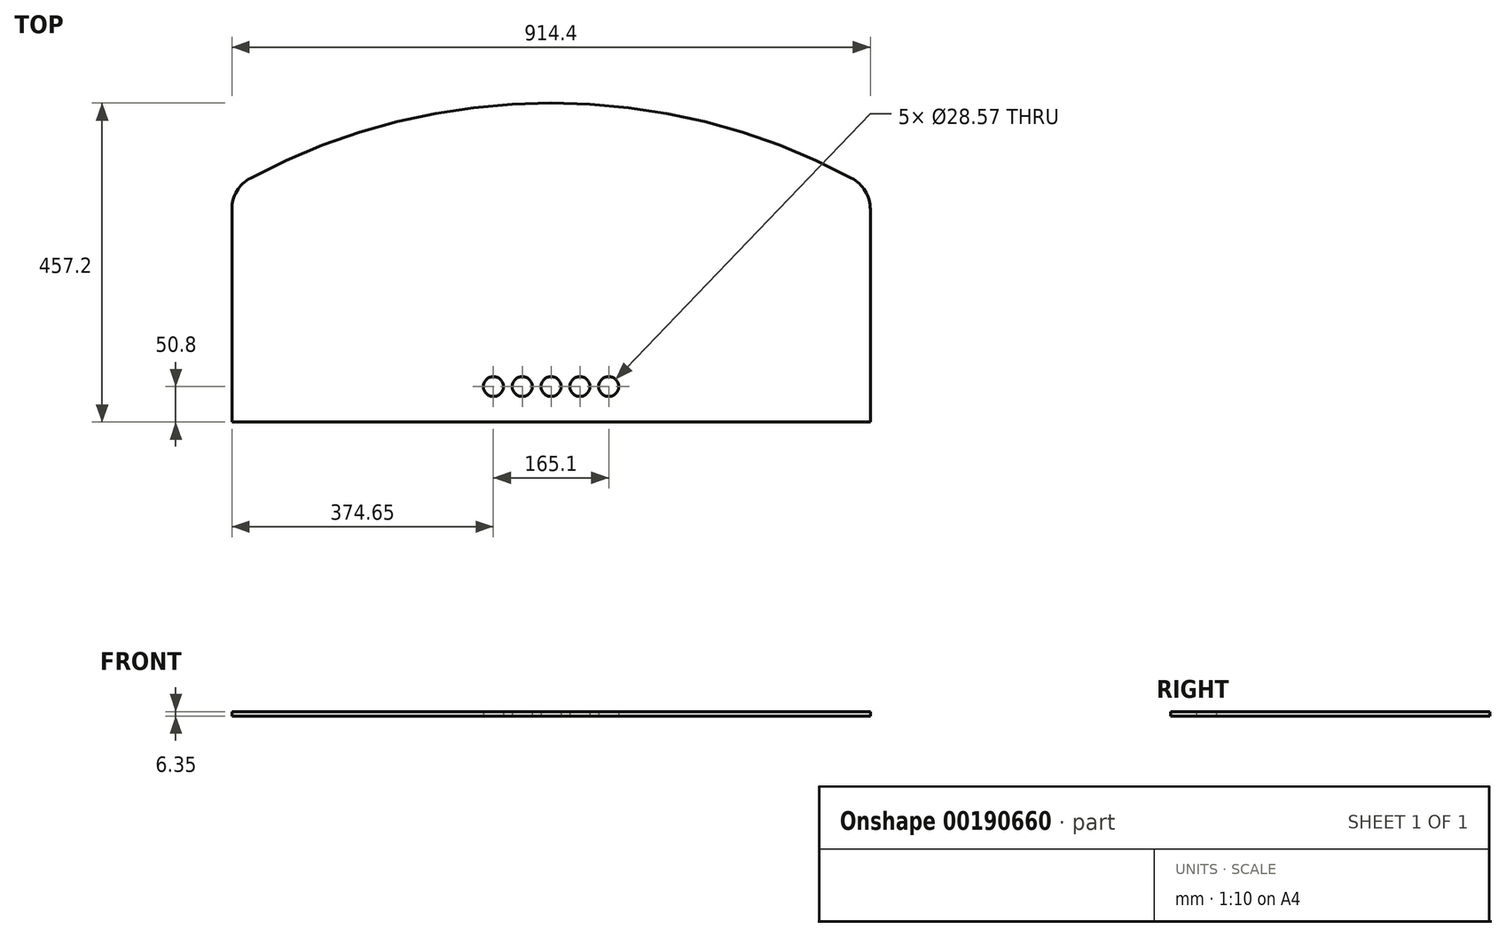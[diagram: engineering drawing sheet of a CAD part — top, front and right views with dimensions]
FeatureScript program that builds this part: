
annotation { "Feature Type Name" : "Feature", "Feature Type Description" : "" }
export const myFeature = defineFeature(function(context is Context, id is Id, definition is map)
    precondition{}
    {
        {
            var Q0;
            Q0=qCreatedBy(makeId("Top.planeOp"),FACE);
            var sketch = newSketch(context, id + "F0", { "sketchPlane" : qUnion([Q0])});
            skLineSegment(sketch, "E0.bottom", {"start": v(0, 0) * mm, "end": v(-914.4, 0) * mm});
            skLineSegment(sketch, "E0.left", {"start": v(0, 0) * mm, "end": v(0, 304.8) * mm});
            skLineSegment(sketch, "E0.right", {"start": v(-914.4, 0) * mm, "end": v(-914.4, 304.8) * mm});
            skArc(sketch, "E1", {"start": v(-26.9, 349.62) * mm, "mid": v(-457.2, 457.2) * mm, "end": v(-887.5, 349.62) * mm});
            skArc(sketch, "E2.filletArc", {"start": v(-887.5, 349.62) * mm, "mid": v(-907.16, 330.94) * mm, "end": v(-914.4, 304.8) * mm});
            skArc(sketch, "E3.filletArc", {"start": v(0, 304.8) * mm, "mid": v(-7.24, 330.94) * mm, "end": v(-26.9, 349.62) * mm});
            skLineSegment(sketch, "E4", {"start": v(-457.2, 0) * mm, "end": v(-457.2, 457.2) * mm, "construction": true});
            skSolve(sketch);
        }
        {
            var Q0;
            Q0=makeQuery(id+"F0.imprint","IMPRINT",FACE,{"disambiguationData":[TD([[makeQuery(id+"F0.imprint","IMPRINT",EDGE,{"derivedFrom":sQuery(id+"F0.wireOp",EDGE,"E0.bottom")}),-1.0]])]});
            extrude(context, id + "F1", {"entities" : qUnion([Q0]), "depth" : 6.35 * mm});
        }
        {
            var Q0;
            Q0=qCreatedBy(makeId("Top.planeOp"),FACE);
            var sketch = newSketch(context, id + "F2", { "sketchPlane" : qUnion([Q0])});
            skLineSegment(sketch, "E5", {"start": v(0, 0) * mm, "end": v(-914.4, 0) * mm, "construction": true});
            skLineSegment(sketch, "E6", {"start": v(-457.2, 0) * mm, "end": v(-457.2, 457.2) * mm, "construction": true});
            skPoint(sketch, "E6.endSnap0", {"position": v(-457.2, 0) * mm});
            skLineSegment(sketch, "E7", {"start": v(0, 0) * mm, "end": v(0, 304.8) * mm, "construction": true});
            skLineSegment(sketch, "E8", {"start": v(0, 304.8) * mm, "end": v(-914.4, 304.8) * mm, "construction": true});
            skLineSegment(sketch, "E9", {"start": v(0, 0) * mm, "end": v(0, 50.8) * mm, "construction": true});
            skLineSegment(sketch, "E10", {"start": v(0, 50.8) * mm, "end": v(-914.4, 50.8) * mm, "construction": true});
            skPoint(sketch, "E11", {"position": v(-457.2, 50.8) * mm});
            skPoint(sketch, "E12", {"position": v(-415.93, 50.8) * mm});
            skPoint(sketch, "E13", {"position": v(-374.65, 50.8) * mm});
            skPoint(sketch, "E14", {"position": v(-498.48, 50.8) * mm});
            skPoint(sketch, "E15", {"position": v(-539.75, 50.8) * mm});
            skLineSegment(sketch, "E16", {"start": v(-914.4, 304.8) * mm, "end": v(-457.2, 457.2) * mm, "construction": true});
            skSolve(sketch);
        }
        {
            var Q0;
            Q0=sQuery(id+"F2.wireOp",VERTEX,"E12");
            var Q1;
            Q1=sQuery(id+"F2.wireOp",VERTEX,"E13");
            var Q2;
            Q2=sQuery(id+"F2.wireOp",VERTEX,"E11");
            var Q3;
            Q3=sQuery(id+"F2.wireOp",VERTEX,"E14");
            var Q4;
            Q4=sQuery(id+"F2.wireOp",VERTEX,"E15");
            var Q5;
            Q5=makeQuery(id+"F1.opExtrude","SWEPT_BODY",BODY,{"disambiguationData":[OSD([sQuery(id+"F0.wireOp",EDGE,"E0.bottom"),sQuery(id+"F0.wireOp",EDGE,"E0.left"),sQuery(id+"F0.wireOp",EDGE,"E0.right"),sQuery(id+"F0.wireOp",EDGE,"E1"),sQuery(id+"F0.wireOp",EDGE,"E2.filletArc"),sQuery(id+"F0.wireOp",EDGE,"E3.filletArc")])]});
            hole(context, id + "F3", {"style" : HoleStyle.SIMPLE, "endStyle" : HoleEndStyle.THROUGH, "oppositeDirection" : true, "holeDiameter" : 28.57 * mm, "locations" : qUnion([Q0, Q1, Q2, Q3, Q4]), "scope" : qUnion([Q5]), "isTappedThrough" : true});
        }
    });
